# Revit family: LME_model_7ft9in-9ft4in
name_source: partatom
category: Generic Models
units: mm (PartAtom-declared; Revit-internal decimal feet)

## family parameters
Always vertical = Yes
Can host rebar = No
Cut with Voids When Loaded = No
Host = Floor
Maintain Annotation Orientation = No
Part Type = Undefined
Room Calculation Point = No
Round Connector Dimension = Use Diameter
Shared = No

## types (2) — shared parameters
Assembly Code = C2010130
BIMobject Category = Construction - Stairs
Box Material = Pinewood - FAKRO - RAL1013 - Box
Box height = 5 1/2"
Box material_ = Pine
Brand url = http://www.fakro.com
CSI MasterFormat 2016 Code = 05 51 33
CSI MasterFormat 2016 Title = Metal Ladders
Ceiling height = 7'9" - 9'4"
Default Elevation = 0"
Description = Metal folding attic ladders
Design country = Poland
Folded ladder height = 10"
Handrail Material = Aluminium - FAKRO - RAL3020 - Handrail
Hatch Material = Pinewood - FAKRO - RAL9003 - Hatch
Hatch colour = White
Hatch thickness = 1 3/8"
Hole width = 3/8"
IFC Classification = Stair
Insulation thickness = 1 1/8"
Ladder Material = Aluminium - FAKRO - RAL7022 - Ladder
Ladder material = Metal
Landing space = 40" - 47"
Manufacturer = FAKRO
Manufacturer country = Poland
Manufacturer name = FAKRO
Material Actuators = Aluminium - FAKRO - RAL9006 - Actuators
Material main = Metal
Material secondary = Wood
Maximum loading = 400 lbs
Model = LME
Nominal height = 5 1/2"
Nominal length = 47"
OmniClass Code = 21-02 01 08 08
OmniClass Description = Stairs - Ladders
Product Guid = a19cb289-0371-4254-9933-b940d6c35eb9
Product SKU = usa_metal_attic_ladders_lme
Product data url = https://www.bimobject.com
Product family = Loft ladders
Product group = Metal loft ladders
Product url = https://www.fakrousa.com
QR code = http://bimobject.com
R-value = 5.3
Seal Material = Rubber - FAKRO - RAL9005 - Seal
Stile Ends Material = Rubber - FAKRO - RAL9005 - Stile Ends
Technical description = https://www.fakrousa.com
Tread length in the ladder = 13 1/4"
Tread width in the ladder = 3 1/8"
Treads material = Metal
UNSPSC Category = Ladders
UNSPSC Code = 30191501
URL = https://www.fakrousa.com
Uniformat II Code = B1080,80
Uniformat II Description = Stairs - Ladders
Warning = The present model is for informational-demonstrative purposes only and as such cannot constitute a basis for performance. All dimensions presented in this model should be verified on site. Because of the fact that the model is a schematic one, FAKRO shall not assume any responsibility for the actual installation quality on the roof.
Youtube clip = https://www.fakrousa.com

## per-type parameters (varying)
| type | Edition number | Internal box dimension | Nominal width | Obj Type | Weight Net (Kg) | Weight Net (lbs) |
| LME - 22 1/2" x 47" | 1 | 20 1/2" x 44 7/8" | 22 1/2" | 1 | 27 | 60 |
| LME - 25" x 47" | 2 | 23" x 44 7/8" | 25" | 2 | 28 | 62 |

## geometry (parser evidence)
native form markers: Sweep x2
no freeform markers — native parametric forms only
